# Revit family: CCTYP03
name_source: partatom
category: Furniture
units: mm (PartAtom-declared; Revit-internal decimal feet)

## family parameters
Always vertical = Yes
Cut with Voids When Loaded = No
OmniClass Number = 23.40.20.00
OmniClass Title = General Furniture and Specialties
Render Appearance Source = Family Geometry
Room Calculation Point = No
Shared = No
Work Plane-Based = No

## types (1)
- CCTYP03
    Cost = 19549 $
    Default Elevation = 0 mm  [stored 0 ft]
    Description = 1 x Devens Grey Side Chair, 1 x Auburn Ivory Conference Chair - Express, 2 x Rectangular - 2mm Edge - 24D x 60W, 1 x Rectangular - 2mm Edge - 30D x 60W, 1 x Freestanding O-Leg 27" X 30", 1 x U-Channel - 48W, 1 x CBX Full Depth Floor Bookcase 24Dx28Hx30W, 1 x Cbx Suspended Hat Modesty 12h For 60w (44 Actual), 3 x Cbx 2d Full Depth Lat 24dx28hx30w, 2 x CBX Wall Mounted L Shelf Vertical 45Hx60Wx12D
    Exported From CET Designer = Yes
    Manufacturer = AIS
    Model = 4667
    Show CCTYP03 = Yes
    VisibilityIndex = 0

note: [stored X ft] marks values corroborated as IEEE doubles in the binary element streams (Revit-internal decimal feet)

## geometry (parser evidence)
native form markers: Sweep x3
no freeform markers — native parametric forms only
